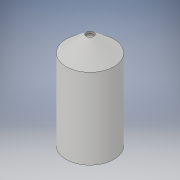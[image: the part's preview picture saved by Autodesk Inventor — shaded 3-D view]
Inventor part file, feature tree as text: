
AUTODESK INVENTOR PART (.ipt)
format: ipt  version: 2018 (Build 220112000, 112)  size: 151,552 bytes
history: native  units: in
note: dims shown in document units (in); Inventor stores cm internally (conversion verified against a paired STEP export)
features: sketch x3, projected_geometry x2, extrude x1, plane x1, revolve x1
ambient origin geometry x8: Origin, YZ Plane, XZ Plane, XY Plane, X Axis, Y Axis, Z Axis, Center Point
bodies: Solid1 (feature_tree)
feature tree (8):
  extrude  "Extrusion1"  Depth=1.0in
  sketch  "Sketch2"  dims[d2=1.0in d7=2.875in]
  plane  "Work Plane2"
  revolve  "Revolution1"  [1 undecoded]
  sketch  "Sketch1"  dims[d0=1.0in d1=1.0in]
  sketch  "Sketch4"  dims[d8=0.25in d9=3.8in d10=0.0in d13=0.0in d14=1.0in d15=1.0in d16=0.2in d17=90.0deg d18=0.1875in d19=0.1in]
  projected_geometry  "Projected Loop1"
  projected_geometry  "Projected Loop2"
note: 1 required parameter value undecoded (feature->parameter linkage not recoverable at this tier; creation-order binding heuristic only, values carry confidence <= 0.55)
